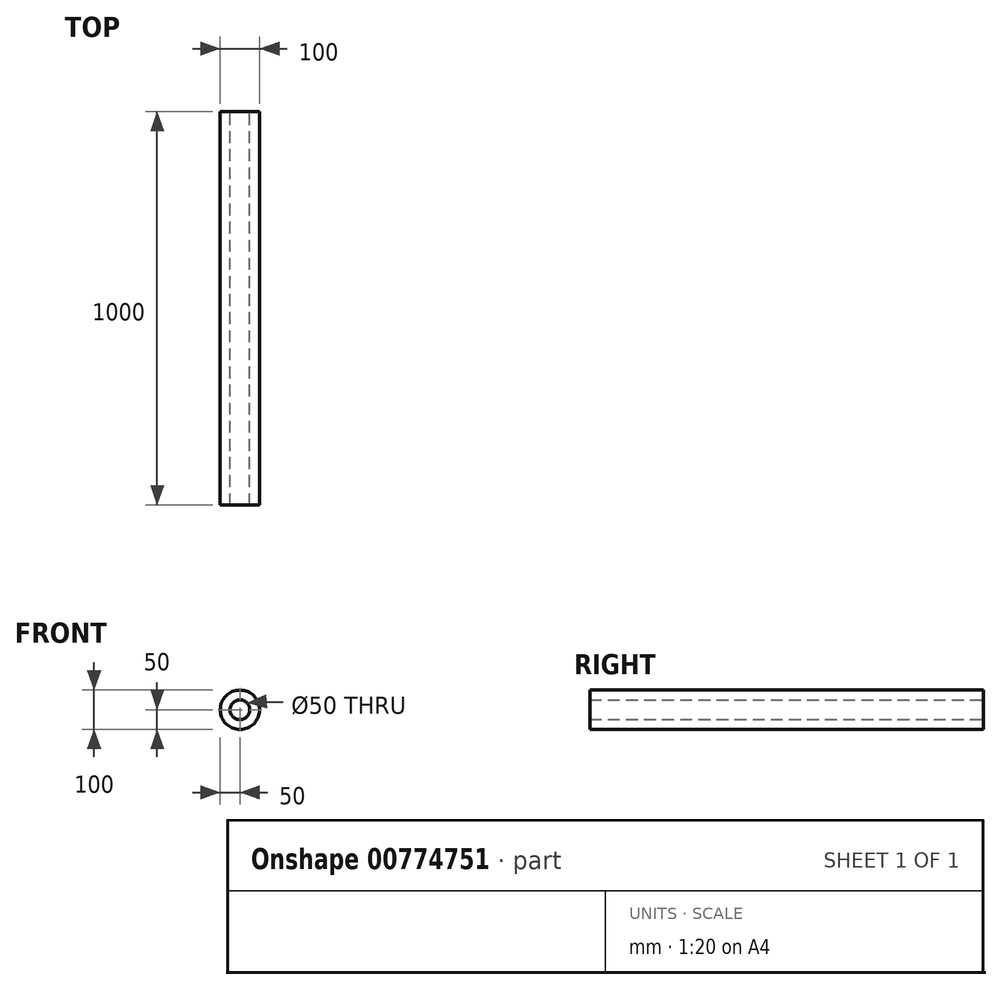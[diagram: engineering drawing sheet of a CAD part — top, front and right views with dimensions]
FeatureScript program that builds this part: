
annotation { "Feature Type Name" : "Feature", "Feature Type Description" : "" }
export const myFeature = defineFeature(function(context is Context, id is Id, definition is map)
    precondition{}
    {
        {
            var Q0;
            Q0=qCreatedBy(makeId("Front.planeOp"),FACE);
            var sketch = newSketch(context, id + "F0", { "sketchPlane" : qUnion([Q0])});
            skCircle(sketch, "E0", {"center": v(0, 0) * mm, "radius": 25 * mm});
            skCircle(sketch, "E1", {"center": v(0, 0) * mm, "radius": 50 * mm});
            skSolve(sketch);
        }
        {
            var Q0;
            Q0=makeQuery(id+"F0.imprint","IMPRINT",FACE,{"disambiguationData":[TD([[makeQuery(id+"F0.imprint","IMPRINT",EDGE,{"derivedFrom":sQuery(id+"F0.wireOp",EDGE,"E0")}),-1.0]])]});
            extrude(context, id + "F1", {"entities" : qUnion([Q0]), "depth" : 1000 * mm, "offsetDistance" : 25 * mm});
        }
    });
